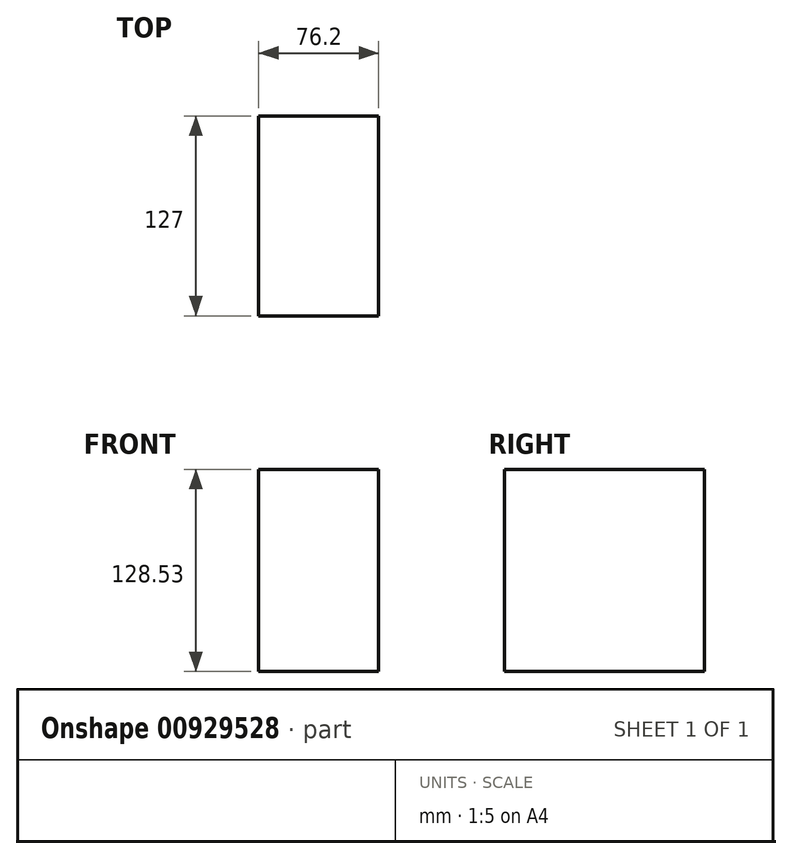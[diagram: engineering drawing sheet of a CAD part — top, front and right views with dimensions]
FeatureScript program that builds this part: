
annotation { "Feature Type Name" : "Feature", "Feature Type Description" : "" }
export const myFeature = defineFeature(function(context is Context, id is Id, definition is map)
    precondition{}
    {
        {
            var Q0;
            Q0=qCreatedBy(makeId("Right.planeOp"),FACE);
            var sketch = newSketch(context, id + "F0", { "sketchPlane" : qUnion([Q0])});
            skLineSegment(sketch, "E0.bottom", {"start": v(0, 0) * mm, "end": v(127, 0) * mm});
            skLineSegment(sketch, "E0.top", {"start": v(0, 128.53) * mm, "end": v(127, 128.53) * mm});
            skLineSegment(sketch, "E0.left", {"start": v(0, 0) * mm, "end": v(0, 128.53) * mm});
            skLineSegment(sketch, "E0.right", {"start": v(127, 0) * mm, "end": v(127, 128.53) * mm});
            skSolve(sketch);
        }
        {
            var Q0;
            Q0 = qSketchRegion(id + "F0", true);
            extrude(context, id + "F1", {"entities" : qUnion([Q0]), "depth" : 76.2 * mm, "offsetDistance" : 25.4 * mm});
        }
    });
